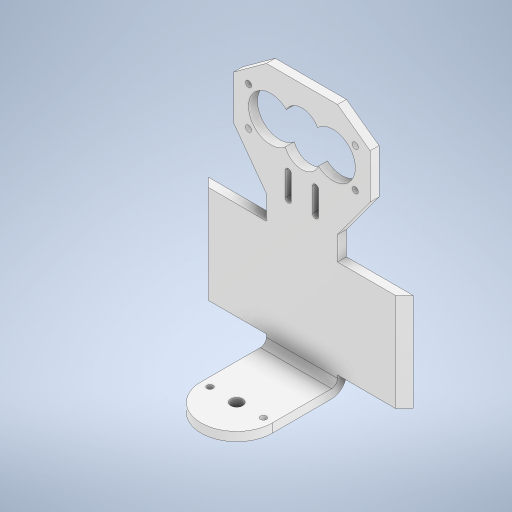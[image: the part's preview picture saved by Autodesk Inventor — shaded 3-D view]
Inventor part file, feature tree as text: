
AUTODESK INVENTOR PART (.ipt)
format: ipt  version: 2023 (Build 270158000, 158)  size: 364,032 bytes
history: native  units: in
note: dims shown in document units (in); Inventor stores cm internally (conversion verified against a paired STEP export)
features: extrude x4, sketch x4, chamfer x2, plane x1
ambient origin geometry x8: Origin, YZ Plane, XZ Plane, XY Plane, X Axis, Y Axis, Z Axis, Center Point
bodies: Solid1 (feature_tree)
feature tree (11):
  extrude  "Extrusion1"  TaperAngle=0.0deg  [1 undecoded]
  extrude  "Extrusion2"  Depth=0.0787in TaperAngle=45.0deg
  extrude  "Extrusion3"  Depth=2.7165in
  chamfer  "Chamfer1"  Distance=0.1181in
  plane  "Work Plane1"
  extrude  "Extrusion4"  Depth=0.1181in TaperAngle=45.0deg
  chamfer  "Chamfer2"  [1 undecoded]
  sketch  "Sketch1"  dims[d0=0.0394in d1=0.0in d7=0.0in d8=0.0in]
  sketch  "Sketch3"  dims[d9=0.0787in d10=0.0in d11=0.0787in d12=0.0787in d13=45.0deg]
  sketch  "Sketch4"  dims[d14=0.0in d15=2.7165in]
  sketch  "Sketch5"  dims[d16=0.0787in d17=0.1181in d18=0.0in d19=0.1181in d20=0.0787in d21=45.0deg]
note: 2 required parameter values undecoded (feature->parameter linkage not recoverable at this tier; creation-order binding heuristic only, values carry confidence <= 0.55)
